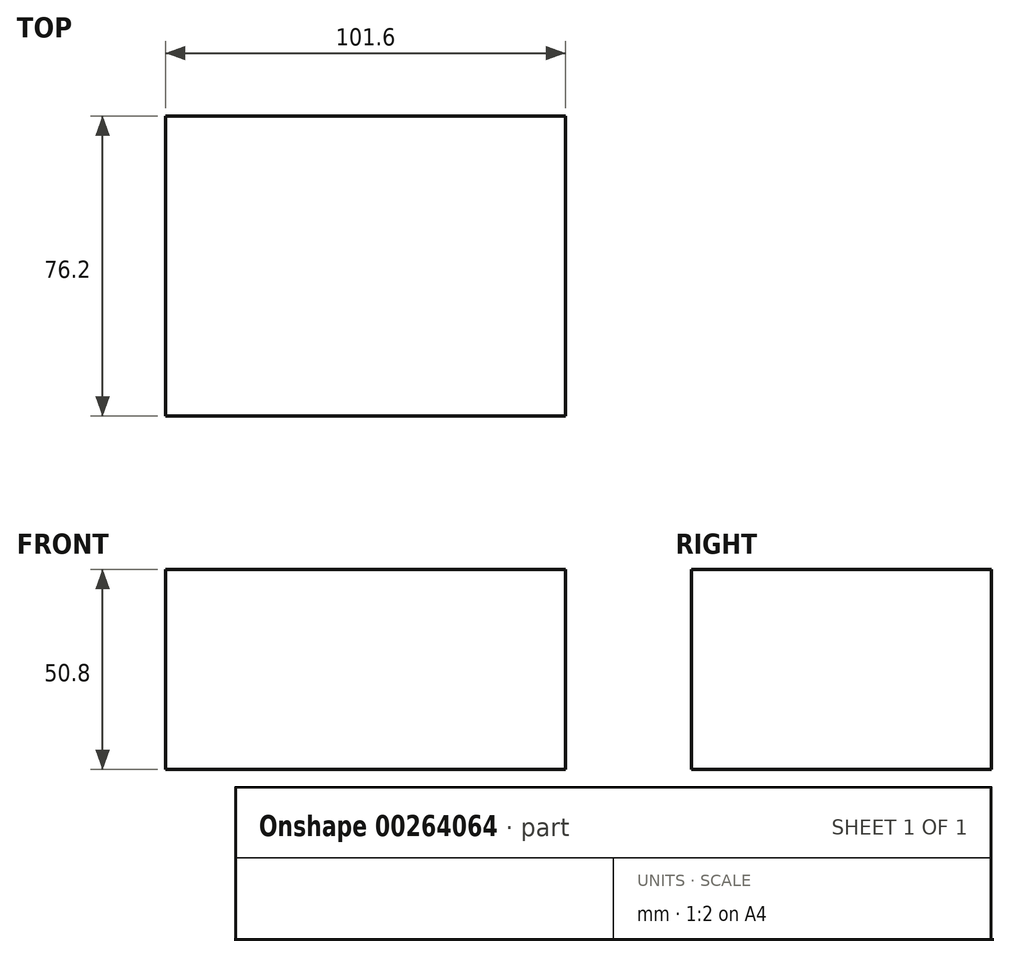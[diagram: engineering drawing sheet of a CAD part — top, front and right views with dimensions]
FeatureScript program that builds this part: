
annotation { "Feature Type Name" : "Feature", "Feature Type Description" : "" }
export const myFeature = defineFeature(function(context is Context, id is Id, definition is map)
    precondition{}
    {
        {
            var Q0;
            Q0=qCreatedBy(makeId("Front.planeOp"),FACE);
            var sketch = newSketch(context, id + "F0", { "sketchPlane" : qUnion([Q0])});
            skLineSegment(sketch, "E0.bottom", {"start": v(0, 0) * mm, "end": v(101.6, 0) * mm});
            skLineSegment(sketch, "E0.top", {"start": v(0, 50.8) * mm, "end": v(101.6, 50.8) * mm});
            skLineSegment(sketch, "E0.left", {"start": v(0, 0) * mm, "end": v(0, 50.8) * mm});
            skLineSegment(sketch, "E0.right", {"start": v(101.6, 0) * mm, "end": v(101.6, 50.8) * mm});
            skSolve(sketch);
        }
        {
            var Q0;
            Q0 = qSketchRegion(id + "F0", true);
            extrude(context, id + "F1", {"entities" : qUnion([Q0]), "depth" : 76.2 * mm});
        }
    });
